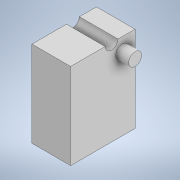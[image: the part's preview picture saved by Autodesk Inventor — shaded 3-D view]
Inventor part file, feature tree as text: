
AUTODESK INVENTOR PART (.ipt)
format: ipt  version: 2021 (Build 250183000, 183)  size: 161,792 bytes
history: native  units: mm
features: extrude x6, sketch x6, emboss x1
ambient origin geometry x8: Origin, YZ Plane, XZ Plane, XY Plane, X Axis, Y Axis, Z Axis, Center Point
bodies: Solid1 (feature_tree)
feature tree (13):
  extrude  "Extrusion1"  Depth=10.5655mm
  extrude  "Extrusion3"  Depth=9.0mm TaperAngle=0.0deg
  emboss  "Emboss1"
  extrude  "Extrusion5"  Depth=3.0mm TaperAngle=0.0deg
  extrude  "Extrusion6"  Depth=1.0mm
  extrude  "Extrusion9"  Depth=0.517mm TaperAngle=0.0deg
  extrude  "Extrusion10"  Depth=3.0mm
  sketch  "Sketch1"  dims[d0=21.131mm d2=10.5655mm]
  sketch  "Sketch4"  dims[d3=7.5mm d4=9.0mm d5=0.0mm]
  sketch  "Sketch6"  dims[d12=3.0mm d15=3.0mm d16=0.0mm]
  sketch  "Sketch7"  dims[d17=1.0mm d18=0.0mm d27=14.483mm]
  sketch  "Sketch10"  dims[d28=0.174mm d29=0.0mm d30=0.517mm d31=0.0mm]
  sketch  "Sketch11"  dims[d38=1.302mm d39=0.0mm d40=3.0mm d41=9.519mm d42=0.0mm d43=0.0mm]
